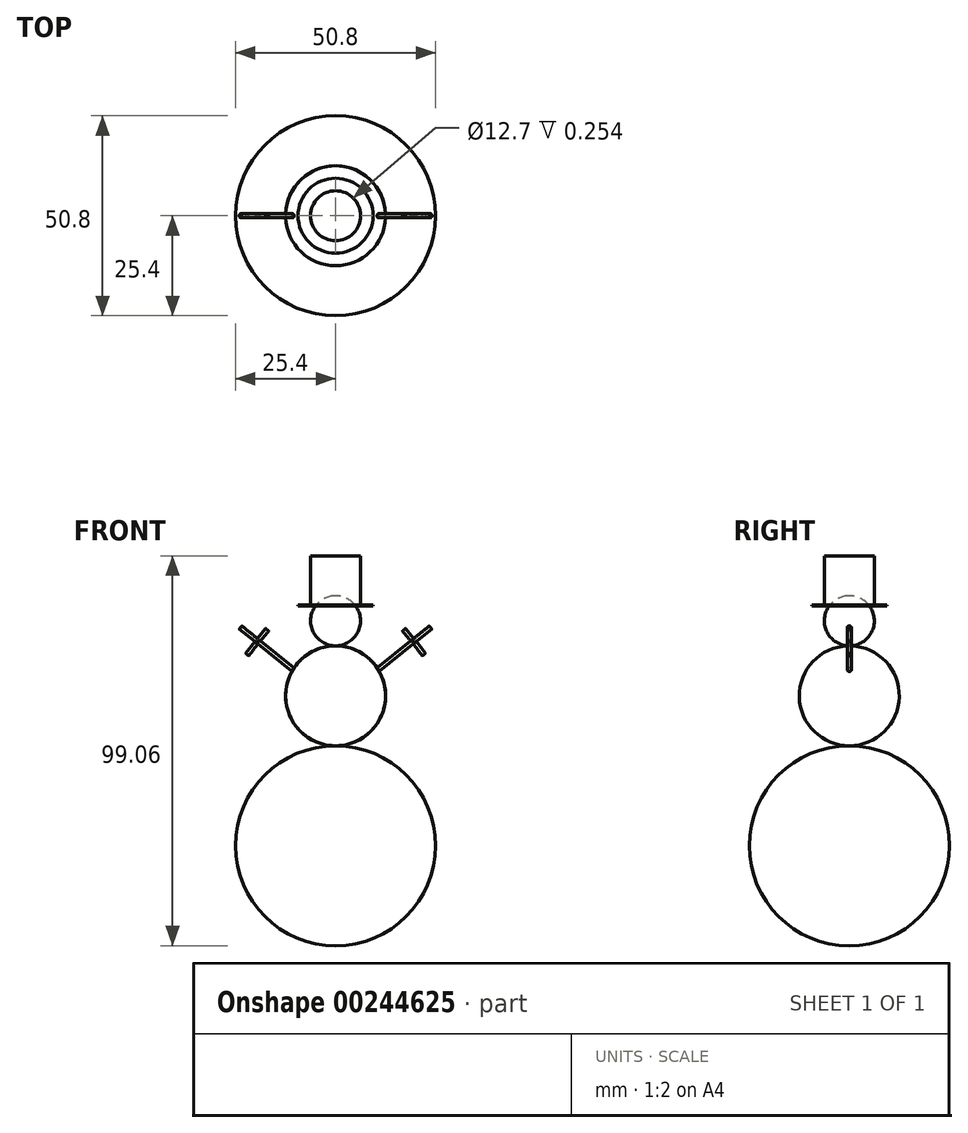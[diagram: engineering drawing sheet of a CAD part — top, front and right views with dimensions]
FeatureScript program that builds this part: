
annotation { "Feature Type Name" : "Feature", "Feature Type Description" : "" }
export const myFeature = defineFeature(function(context is Context, id is Id, definition is map)
    precondition{}
    {
        {
            var Q0;
            Q0=qCreatedBy(makeId("Front.planeOp"),FACE);
            var sketch = newSketch(context, id + "F0", { "sketchPlane" : qUnion([Q0])});
            skLineSegment(sketch, "E0", {"start": v(0, 0) * mm, "end": v(0, -50.8) * mm});
            skLineSegment(sketch, "E1", {"start": v(0, 0) * mm, "end": v(0, 25.4) * mm});
            skLineSegment(sketch, "E2", {"start": v(0, 25.4) * mm, "end": v(0, 38.1) * mm});
            skCircle(sketch, "E3", {"center": v(0, -25.4) * mm, "radius": 25.4 * mm});
            skCircle(sketch, "E4", {"center": v(0, 12.7) * mm, "radius": 12.7 * mm});
            skCircle(sketch, "E5", {"center": v(0, 31.75) * mm, "radius": 6.35 * mm});
            skSolve(sketch);
        }
        {
            var Q0;
            {var subQ0=sQuery(id+"F0.wireOp",EDGE,"E2");Q0=makeQuery(id+"F0.imprint","IMPRINT",FACE,{"disambiguationData":[TD([[makeQuery(id+"F0.imprint","IMPRINT",EDGE,{"derivedFrom":subQ0}),1.0]])]});}
            var Q1;
            {var subQ0=sQuery(id+"F0.wireOp",EDGE,"E1");Q1=makeQuery(id+"F0.imprint","IMPRINT",FACE,{"disambiguationData":[TD([[makeQuery(id+"F0.imprint","IMPRINT",EDGE,{"derivedFrom":subQ0}),1.0]])]});}
            var Q2;
            {var subQ0=sQuery(id+"F0.wireOp",EDGE,"E0");Q2=makeQuery(id+"F0.imprint","IMPRINT",FACE,{"disambiguationData":[TD([[makeQuery(id+"F0.imprint","IMPRINT",EDGE,{"derivedFrom":subQ0}),-1.0]])]});}
            var Q3;
            Q3=sQuery(id+"F0.wireOp",EDGE,"E1");
            revolve(context, id + "F1", {"entities" : qUnion([Q0, Q1, Q2]), "axis" : qUnion([Q3]), "revolveType" : RevolveType.FULL});
        }
        {
            var Q0;
            Q0=qCreatedBy(makeId("Top.planeOp"),FACE);
            cPlane(context, id + "F2", {"entities" : qUnion([Q0]), "cplaneType" : CPlaneType.OFFSET, "offset" : 35.56 * mm, "width" : 152.4 * mm, "height" : 152.4 * mm});
        }
        {
            var Q0;
            Q0=qCreatedBy(id+"F2.planeOp",FACE);
            var sketch = newSketch(context, id + "F3", { "sketchPlane" : qUnion([Q0])});
            skCircle(sketch, "E6", {"center": v(0, 0) * mm, "radius": 9.53 * mm});
            skCircle(sketch, "E7", {"center": v(0, 0) * mm, "radius": 6.35 * mm});
            skSolve(sketch);
        }
        {
            var Q0;
            Q0=makeQuery(id+"F3.imprint","IMPRINT",FACE,{"disambiguationData":[TD([[makeQuery(id+"F3.imprint","IMPRINT",EDGE,{"derivedFrom":sQuery(id+"F3.wireOp",EDGE,"E6")}),1.0]])]});
            extrude(context, id + "F4", {"entities" : qUnion([Q0]), "depth" : 0.25 * mm});
        }
        {
            var Q0;
            Q0=makeQuery(id+"F3.imprint","IMPRINT",FACE,{"disambiguationData":[TD([[makeQuery(id+"F3.imprint","IMPRINT",EDGE,{"derivedFrom":sQuery(id+"F3.wireOp",EDGE,"E7")}),1.0]])]});
            extrude(context, id + "F5", {"entities" : qUnion([Q0]), "depth" : 12.7 * mm});
        }
        {
            var Q0;
            Q0=qCreatedBy(makeId("Front.planeOp"),FACE);
            var sketch = newSketch(context, id + "F6", { "sketchPlane" : qUnion([Q0])});
            skLineSegment(sketch, "E8", {"start": v(0, 10.6) * mm, "end": v(19.78, 26.54) * mm});
            skLineSegment(sketch, "E9", {"start": v(20.11, 26.15) * mm, "end": v(0.32, 10.21) * mm});
            skLineSegment(sketch, "E10", {"start": v(0.32, 10.21) * mm, "end": v(0, 10.6) * mm});
            skLineSegment(sketch, "E11", {"start": v(19.78, 26.54) * mm, "end": v(17.4, 29.5) * mm});
            skLineSegment(sketch, "E12", {"start": v(17.4, 29.5) * mm, "end": v(17.8, 29.82) * mm});
            skLineSegment(sketch, "E13", {"start": v(17.8, 29.82) * mm, "end": v(20.18, 26.86) * mm});
            skLineSegment(sketch, "E14", {"start": v(20.18, 26.86) * mm, "end": v(24.14, 30.05) * mm});
            skLineSegment(sketch, "E15", {"start": v(24.14, 30.05) * mm, "end": v(24.46, 29.65) * mm});
            skLineSegment(sketch, "E16", {"start": v(24.46, 29.65) * mm, "end": v(20.5, 26.47) * mm});
            skLineSegment(sketch, "E17", {"start": v(20.5, 26.47) * mm, "end": v(22.9, 23.5) * mm});
            skLineSegment(sketch, "E18", {"start": v(22.9, 23.5) * mm, "end": v(22.5, 23.18) * mm});
            skLineSegment(sketch, "E19", {"start": v(22.5, 23.18) * mm, "end": v(20.11, 26.15) * mm});
            skLineSegment(sketch, "E20", {"start": v(19.78, 26.54) * mm, "end": v(20.11, 26.15) * mm});
            skLineSegment(sketch, "E21", {"start": v(19.78, 26.54) * mm, "end": v(20.18, 26.86) * mm});
            skLineSegment(sketch, "E22", {"start": v(20.18, 26.86) * mm, "end": v(20.5, 26.47) * mm});
            skLineSegment(sketch, "E23", {"start": v(20.5, 26.47) * mm, "end": v(20.11, 26.15) * mm});
            skSolve(sketch);
        }
        {
            var Q0;
            Q0=makeQuery(id+"F6.imprint","IMPRINT",FACE,{"disambiguationData":[TD([[makeQuery(id+"F6.imprint","IMPRINT",EDGE,{"derivedFrom":sQuery(id+"F6.wireOp",EDGE,"E8")}),-1.0]])]});
            var Q1;
            Q1=sQuery(id+"F6.wireOp",EDGE,"E8");
            revolve(context, id + "F7", {"operationType" : NewBodyOperationType.ADD, "entities" : qUnion([Q0]), "axis" : qUnion([Q1]), "revolveType" : RevolveType.FULL});
        }
        {
            var Q0;
            Q0=makeQuery(id+"F6.imprint","IMPRINT",FACE,{"disambiguationData":[TD([[makeQuery(id+"F6.imprint","IMPRINT",EDGE,{"derivedFrom":sQuery(id+"F6.wireOp",EDGE,"E11")}),-1.0]])]});
            var Q1;
            Q1=sQuery(id+"F6.wireOp",EDGE,"E11");
            revolve(context, id + "F8", {"operationType" : NewBodyOperationType.ADD, "entities" : qUnion([Q0]), "axis" : qUnion([Q1]), "revolveType" : RevolveType.FULL});
        }
        {
            var Q0;
            Q0=makeQuery(id+"F6.imprint","IMPRINT",FACE,{"disambiguationData":[TD([[makeQuery(id+"F6.imprint","IMPRINT",EDGE,{"derivedFrom":sQuery(id+"F6.wireOp",EDGE,"E17")}),-1.0]])]});
            var Q1;
            Q1=sQuery(id+"F6.wireOp",EDGE,"E19");
            revolve(context, id + "F9", {"operationType" : NewBodyOperationType.ADD, "entities" : qUnion([Q0]), "axis" : qUnion([Q1]), "revolveType" : RevolveType.FULL});
        }
        {
            var Q0;
            Q0=makeQuery(id+"F6.imprint","IMPRINT",FACE,{"disambiguationData":[TD([[makeQuery(id+"F6.imprint","IMPRINT",EDGE,{"derivedFrom":sQuery(id+"F6.wireOp",EDGE,"E20")}),1.0]])]});
            var Q1;
            Q1=makeQuery(id+"F6.imprint","IMPRINT",FACE,{"disambiguationData":[TD([[makeQuery(id+"F6.imprint","IMPRINT",EDGE,{"derivedFrom":sQuery(id+"F6.wireOp",EDGE,"E14")}),-1.0]])]});
            var Q2;
            Q2=sQuery(id+"F6.wireOp",EDGE,"E14");
            revolve(context, id + "F10", {"entities" : qUnion([Q0, Q1]), "axis" : qUnion([Q2]), "revolveType" : RevolveType.FULL});
        }
        {
            var Q0;
            Q0=makeQuery(id+"F1.opRevolve","SWEPT_BODY",BODY,{"disambiguationData":[OSD([sQuery(id+"F0.wireOp",EDGE,"E1"),sQuery(id+"F0.wireOp",EDGE,"E4")])]});
            var Q1;
            Q1=makeQuery(id+"F10.opRevolve","SWEPT_BODY",BODY,{"disambiguationData":[OSD([sQuery(id+"F6.wireOp",EDGE,"E14"),sQuery(id+"F6.wireOp",EDGE,"E15"),sQuery(id+"F6.wireOp",EDGE,"E16"),sQuery(id+"F6.wireOp",EDGE,"E20"),sQuery(id+"F6.wireOp",EDGE,"E21"),sQuery(id+"F6.wireOp",EDGE,"E23")])]});
            var Q2;
            Q2=makeQuery(id+"F9.opRevolve","SWEPT_BODY",BODY,{"disambiguationData":[OSD([sQuery(id+"F6.wireOp",EDGE,"E17"),sQuery(id+"F6.wireOp",EDGE,"E18"),sQuery(id+"F6.wireOp",EDGE,"E19"),sQuery(id+"F6.wireOp",EDGE,"E23")])]});
            var Q3;
            Q3=qCreatedBy(makeId("Right.planeOp"),FACE);
            mirror(context, id + "F11", {"operationType" : NewBodyOperationType.ADD, "entities" : qUnion([Q0, Q1, Q2]), "mirrorPlane" : qUnion([Q3])});
        }
    });
